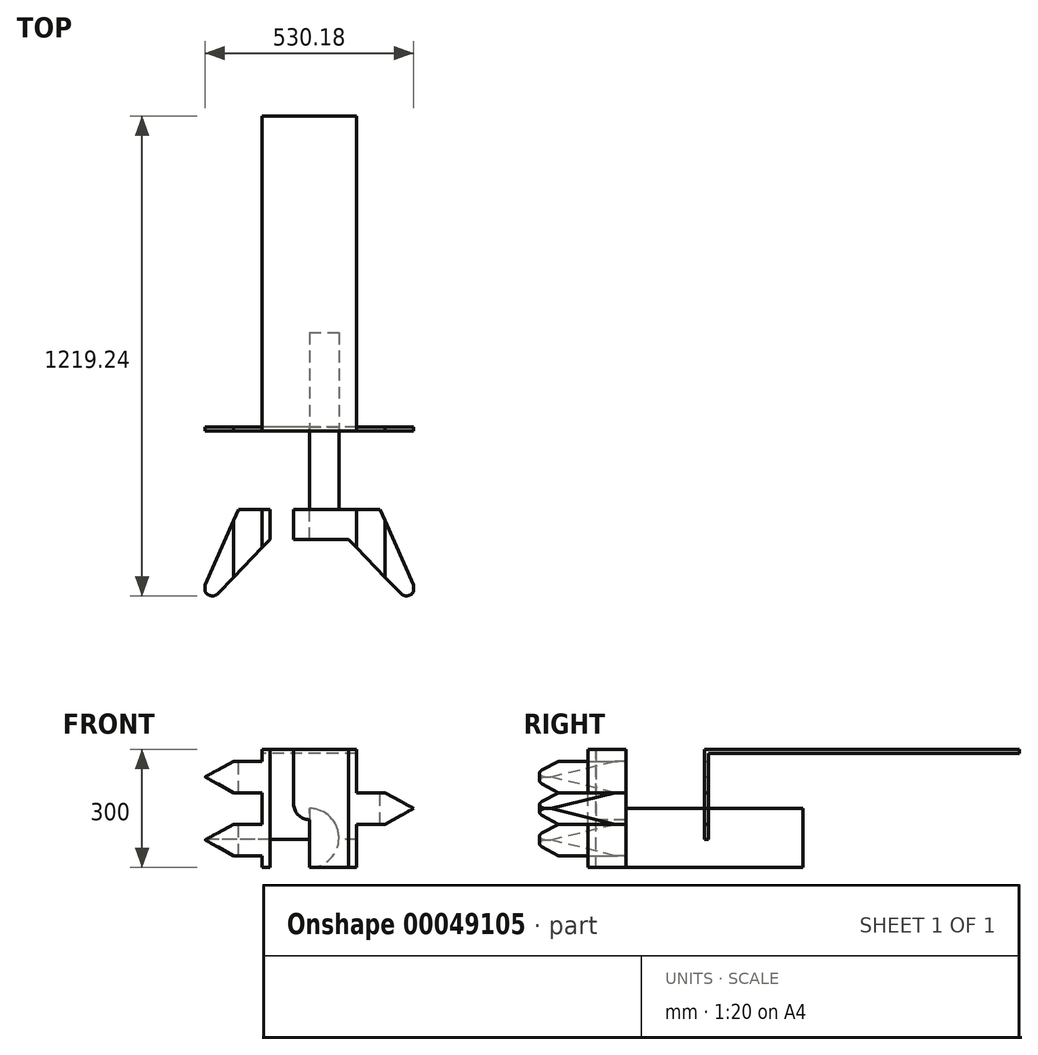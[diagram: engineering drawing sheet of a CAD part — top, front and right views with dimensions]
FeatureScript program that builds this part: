
annotation { "Feature Type Name" : "Feature", "Feature Type Description" : "" }
export const myFeature = defineFeature(function(context is Context, id is Id, definition is map)
    precondition{}
    {
        {
            var Q0;
            Q0=qCreatedBy(makeId("Top.planeOp"),FACE);
            cPlane(context, id + "F0", {"entities" : qUnion([Q0]), "cplaneType" : CPlaneType.OFFSET, "offset" : 1200 * mm, "oppositeDirection" : true, "width" : 150 * mm, "height" : 150 * mm});
        }
        {
            var Q0;
            Q0=qCreatedBy(id+"F0.planeOp",FACE);
            var sketch = newSketch(context, id + "F1", { "sketchPlane" : qUnion([Q0])});
            skLineSegment(sketch, "E0.rect.bottom", {"start": v(1150, -800) * mm, "end": v(-1150, -800) * mm});
            skLineSegment(sketch, "E0.rect.top", {"start": v(1150, 16878.4) * mm, "end": v(-1150, 16878.4) * mm});
            skLineSegment(sketch, "E0.rect.left", {"start": v(1150, -800) * mm, "end": v(1150, 16878.4) * mm});
            skLineSegment(sketch, "E0.rect.right", {"start": v(-1150, -800) * mm, "end": v(-1150, 16878.4) * mm});
            skPoint(sketch, "E0.rect.middle", {"position": v(0, 8039.2) * mm});
            skSolve(sketch);
        }
        {
            var Q0;
            Q0=makeQuery(id+"F1.imprint","IMPRINT",FACE,{"disambiguationData":[TD([[makeQuery(id+"F1.imprint","IMPRINT",EDGE,{"derivedFrom":sQuery(id+"F1.wireOp",EDGE,"E0.rect.bottom")}),-1.0]])]});
            extrude(context, id + "F2", {"entities" : qUnion([Q0]), "oppositeDirection" : true, "depth" : 228.6 * mm});
        }
        {
            var Q0;
            Q0=makeQuery(id+"F2.opExtrude","CAP_FACE",FACE,{"disambiguationData":[OSD([sQuery(id+"F1.wireOp",EDGE,"E0.rect.bottom"),sQuery(id+"F1.wireOp",EDGE,"E0.rect.top"),sQuery(id+"F1.wireOp",EDGE,"E0.rect.left"),sQuery(id+"F1.wireOp",EDGE,"E0.rect.right")])],"isStart":false});
            shell(context, id + "F3", {"entities" : qUnion([Q0]), "thickness" : 10 * mm});
        }
        {
            var Q0;
            Q0=makeQuery(id+"F2.opExtrude","CAP_FACE",FACE,{"disambiguationData":[OSD([sQuery(id+"F1.wireOp",EDGE,"E0.rect.bottom"),sQuery(id+"F1.wireOp",EDGE,"E0.rect.top"),sQuery(id+"F1.wireOp",EDGE,"E0.rect.left"),sQuery(id+"F1.wireOp",EDGE,"E0.rect.right")])],"isStart":true});
            var sketch = newSketch(context, id + "F4", { "sketchPlane" : qUnion([Q0])});
            skLineSegment(sketch, "E1", {"start": v(0, -1076) * mm, "end": v(-100, -1076) * mm});
            skLineSegment(sketch, "E2", {"start": v(-100, -1076) * mm, "end": v(-232.43, -1213.13) * mm});
            skLineSegment(sketch, "E3", {"start": v(-265.09, -1191.1) * mm, "end": v(-180, -1000) * mm});
            skLineSegment(sketch, "E4", {"start": v(-180, -1000) * mm, "end": v(0, -1000) * mm});
            skLineSegment(sketch, "E5", {"start": v(0, -1000) * mm, "end": v(0, -1076) * mm});
            skPoint(sketch, "E6.visualSharp", {"position": v(-311.22, -1294.72) * mm});
            skArc(sketch, "E6.filletArc", {"start": v(-265.09, -1191.1) * mm, "mid": v(-258, -1215.82) * mm, "end": v(-232.43, -1213.13) * mm});
            skSolve(sketch);
        }
        {
            var Q0;
            Q0=qCreatedBy(makeId("Front.planeOp"),FACE);
            var sketch = newSketch(context, id + "F5", { "sketchPlane" : qUnion([Q0])});
            skLineSegment(sketch, "E7.rect.bottom", {"start": v(-192.54, -1470) * mm, "end": v(-120, -1470) * mm});
            skLineSegment(sketch, "E7.rect.top", {"start": v(-192.54, -1230) * mm, "end": v(-120, -1230) * mm});
            skPoint(sketch, "E7.rect.middle", {"position": v(0, -1350) * mm});
            skLineSegment(sketch, "E8.rect.bottom", {"start": v(-192.54, -1310) * mm, "end": v(-120, -1310) * mm});
            skLineSegment(sketch, "E8.rect.top", {"start": v(-192.54, -1390) * mm, "end": v(-120, -1390) * mm});
            skLineSegment(sketch, "E9.rect.bottom", {"start": v(120, -1500) * mm, "end": v(-120, -1500) * mm});
            skLineSegment(sketch, "E9.rect.top", {"start": v(120, -1200) * mm, "end": v(-120, -1200) * mm});
            skLineSegment(sketch, "E9.rect.left", {"start": v(120, -1500) * mm, "end": v(120, -1390) * mm});
            skLineSegment(sketch, "E9.rect.right", {"start": v(-120, -1500) * mm, "end": v(-120, -1470) * mm});
            skLineSegment(sketch, "E10.trimOffspring", {"start": v(120, -1310) * mm, "end": v(192.54, -1310) * mm});
            skLineSegment(sketch, "E11.trimOffspring", {"start": v(120, -1390) * mm, "end": v(192.54, -1390) * mm});
            skPoint(sketch, "E12.trimOffspring.end.orphan", {"position": v(265.09, -1230) * mm});
            skPoint(sketch, "E13.trimOffspring.end.orphan", {"position": v(265.09, -1470) * mm});
            skPoint(sketch, "E14.orphan", {"position": v(-356.46, -1310) * mm});
            skPoint(sketch, "E15.orphan", {"position": v(-356.46, -1390) * mm});
            skLineSegment(sketch, "E16", {"start": v(-192.54, -1230) * mm, "end": v(-265.09, -1270) * mm});
            skLineSegment(sketch, "E17", {"start": v(-265.09, -1270) * mm, "end": v(-192.54, -1310) * mm});
            skLineSegment(sketch, "E18", {"start": v(-192.54, -1390) * mm, "end": v(-265.09, -1430) * mm});
            skLineSegment(sketch, "E19", {"start": v(-265.09, -1430) * mm, "end": v(-192.54, -1470) * mm});
            skLineSegment(sketch, "E20", {"start": v(192.54, -1310) * mm, "end": v(265.09, -1350) * mm});
            skLineSegment(sketch, "E21", {"start": v(265.09, -1350) * mm, "end": v(192.54, -1390) * mm});
            skPoint(sketch, "E22.orphan", {"position": v(265.09, -1390) * mm});
            skPoint(sketch, "E7.rect.right.end.orphan", {"position": v(265.09, -1310) * mm});
            skPoint(sketch, "E8.rect.right.end.orphan", {"position": v(356.46, -1390) * mm});
            skPoint(sketch, "E8.rect.right.start.orphan", {"position": v(356.46, -1310) * mm});
            skPoint(sketch, "E23.orphan", {"position": v(-265.09, -1230) * mm});
            skPoint(sketch, "E24.trimOffspring.start.orphan", {"position": v(-265.09, -1310) * mm});
            skPoint(sketch, "E25.orphan", {"position": v(-265.09, -1390) * mm});
            skPoint(sketch, "E26.orphan", {"position": v(-265.09, -1470) * mm});
            skLineSegment(sketch, "E27.trimOffspring", {"start": v(-120, -1230) * mm, "end": v(-120, -1200) * mm});
            skLineSegment(sketch, "E28.trimOffspring", {"start": v(-120, -1390) * mm, "end": v(-120, -1310) * mm});
            skLineSegment(sketch, "E29.trimOffspring", {"start": v(120, -1310) * mm, "end": v(120, -1200) * mm});
            skSolve(sketch);
        }
        {
            var Q0;
            Q0=makeQuery(id+"F4.imprint","IMPRINT",FACE,{"disambiguationData":[TD([[makeQuery(id+"F4.imprint","IMPRINT",EDGE,{"derivedFrom":sQuery(id+"F4.wireOp",EDGE,"E1")}),-1.0]])]});
            extrude(context, id + "F6", {"entities" : qUnion([Q0]), "oppositeDirection" : true, "depth" : 400 * mm, "hasSecondDirection" : true, "secondDirectionOppositeDirection" : false, "secondDirectionDepth" : 100 * mm});
        }
        {
            var Q0;
            Q0=makeQuery(id+"F6.opExtrude","SWEPT_BODY",BODY,{"disambiguationData":[OSD([sQuery(id+"F4.wireOp",EDGE,"E1"),sQuery(id+"F4.wireOp",EDGE,"E2"),sQuery(id+"F4.wireOp",EDGE,"E3"),sQuery(id+"F4.wireOp",EDGE,"E4"),sQuery(id+"F4.wireOp",EDGE,"E5"),sQuery(id+"F4.wireOp",EDGE,"E6.filletArc")])]});
            var Q1;
            Q1=qCreatedBy(makeId("Right.planeOp"),FACE);
            mirror(context, id + "F7", {"operationType" : NewBodyOperationType.ADD, "entities" : qUnion([Q0]), "mirrorPlane" : qUnion([Q1])});
        }
        {
            var Q0;
            Q0=makeQuery(id+"F5.imprint","IMPRINT",FACE,{"disambiguationData":[TD([[makeQuery(id+"F5.imprint","IMPRINT",EDGE,{"derivedFrom":sQuery(id+"F5.wireOp",EDGE,"E7.rect.bottom")}),1.0]])]});
            extrude(context, id + "F8", {"entities" : qUnion([Q0]), "operationType" : NewBodyOperationType.INTERSECT, "endBound" : BoundingType.THROUGH_ALL, "depth" : 25 * mm});
        }
        {
            var Q0;
            {var subQ0=makeQuery(id+"F6.opExtrude","SWEPT_FACE",FACE,{"disambiguationData":[OSD([sQuery(id+"F4.wireOp",EDGE,"E1")])]});Q0=makeQuery(id+"F7.boolean.opBoolean","MERGE",FACE,{"derivedFrom":[subQ0,makeQuery(id+"F7.opPattern","COPY",FACE,{"derivedFrom":subQ0,"instanceName":"1"})]});}
            var sketch = newSketch(context, id + "F9", { "sketchPlane" : qUnion([Q0])});
            skLineSegment(sketch, "E30", {"start": v(0, -1113.01) * mm, "end": v(0, -1338.62) * mm, "construction": true});
            skArc(sketch, "E31.0.startCap", {"start": v(-40, -1113.01) * mm, "mid": v(0, -1073.01) * mm, "end": v(40, -1113.01) * mm});
            skArc(sketch, "E31.0.endCap", {"start": v(40, -1338.62) * mm, "mid": v(0, -1378.62) * mm, "end": v(-40, -1338.62) * mm});
            skLineSegment(sketch, "E31.0.left", {"start": v(40, -1113.01) * mm, "end": v(40, -1338.62) * mm});
            skLineSegment(sketch, "E31.0.right", {"start": v(-40, -1113.01) * mm, "end": v(-40, -1338.62) * mm});
            skSolve(sketch);
        }
        {
            var Q0;
            {var subQ0=sQuery(id+"F9.wireOp",EDGE,"E31.0.endCap");Q0=makeQuery(id+"F9.imprint","IMPRINT",FACE,{"disambiguationData":[TD([[makeQuery(id+"F9.imprint","IMPRINT",EDGE,{"derivedFrom":subQ0}),-1.0]])]});}
            extrude(context, id + "F10", {"entities" : qUnion([Q0]), "operationType" : NewBodyOperationType.REMOVE, "oppositeDirection" : true, "depth" : 100 * mm});
        }
        {
            var Q0;
            {var subQ0=makeQuery(id+"F6.opExtrude","SWEPT_FACE",FACE,{"disambiguationData":[OSD([sQuery(id+"F4.wireOp",EDGE,"E4")])]});Q0=makeQuery(id+"F7.boolean.opBoolean","MERGE",FACE,{"derivedFrom":[subQ0,makeQuery(id+"F7.opPattern","COPY",FACE,{"derivedFrom":subQ0,"instanceName":"1"})]});}
            var sketch = newSketch(context, id + "F11", { "sketchPlane" : qUnion([Q0])});
            skCircle(sketch, "E32", {"center": v(0, -1425) * mm, "radius": 75 * mm});
            skSolve(sketch);
        }
        {
            var Q0;
            {var subQ0=sQuery(id+"F11.wireOp",EDGE,"E32");var subQ1=makeQuery(id+"F6.opExtrude","SWEPT_FACE",FACE,{"disambiguationData":[OSD([sQuery(id+"F4.wireOp",EDGE,"E4")])]});var subQ2=makeQuery(id+"F7.boolean.opBoolean","MERGE",FACE,{"derivedFrom":[subQ1,makeQuery(id+"F7.opPattern","COPY",FACE,{"derivedFrom":subQ1,"instanceName":"1"})]});var subQ3=makeQuery(id+"F10.boolean.opBoolean","INTERSECT",EDGE,{"derivedFrom":[subQ2,makeQuery(id+"F10.opExtrude","SWEPT_FACE",FACE,{"disambiguationData":[OSD([sQuery(id+"F9.wireOp",EDGE,"E31.0.endCap")])]})]});var subQ4=makeQuery(id+"F11.imprint","INTERSECT",VERTEX,{"disambiguationData":[OD(0.0)],"derivedFrom":[subQ3,subQ0]});Q0=makeQuery(id+"F11.imprint","IMPRINT",FACE,{"disambiguationData":[TD([[makeQuery(id+"F11.imprint","IMPRINT",EDGE,{"disambiguationData":[TD([[subQ4,-1.0]])],"derivedFrom":subQ0}),1.0]])]});}
            extrude(context, id + "F12", {"entities" : qUnion([Q0]), "operationType" : NewBodyOperationType.ADD, "depth" : 450 * mm});
        }
    });
